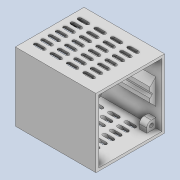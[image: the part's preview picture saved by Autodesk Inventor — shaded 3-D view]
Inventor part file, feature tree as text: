
AUTODESK INVENTOR PART (.ipt)
format: ipt  version: 2021 (Build 250183000, 183)  size: 589,312 bytes
history: native  units: mm
features: extrude x8, sketch x7, projected_geometry x4, plane x3, mirror x2, pattern_linear x1, fillet x1
ambient origin geometry x8: Origin, YZ Plane, XZ Plane, XY Plane, X Axis, Y Axis, Z Axis, Center Point
bodies: Solid1 (feature_tree)
feature tree (26):
  sketch  "Sketch1"  dims[d0=75.0mm d1=75.0mm]
  extrude  "Extrusion1"  Depth=75.0mm
  extrude  "Extrusion2"  TaperAngle=45.0deg  [1 undecoded]
  sketch  "Sketch3"  dims[d2=3.0mm d4=45.0deg]
  plane  "Work Plane1"
  extrude  "Extrusion3"  Depth=60.5mm
  pattern_linear  "Rectangular Pattern1"  Spacing1=85.0mm  [1 undecoded]
  mirror  "Mirror1"
  extrude  "Extrusion4"  Depth=3.0mm TaperAngle=0.0deg
  plane  "Work Plane2"
  sketch  "Sketch7"  dims[d8=56.0mm]
  extrude  "Extrusion5"  Depth=42.5mm
  extrude  "Extrusion6"  [1 undecoded]
  plane  "Work Plane3"
  extrude  "Extrusion8"  Depth=4.0mm
  extrude  "Extrusion9"  Depth=5.0mm
  fillet  "Fillet2"  Radius=33.0mm
  mirror  "Mirror5"
  sketch  "Sketch5"  dims[d5=60.5mm d6=1.8mm]
  sketch  "Sketch6"  dims[d7=1.8mm]
  projected_geometry  "Projected Loop1"
  projected_geometry  "Projected Loop2"
  sketch  "Sketch8"  dims[d9=15.0mm]
  projected_geometry  "Projected Loop3"
  sketch  "Sketch9"  dims[d10=15.0mm d11=85.0mm d12=0.0mm d13=3.0mm d14=0.0mm d16=42.5mm d17=-7.853982mm d19=4.0mm d20=5.0mm d21=33.0mm d22=0.0mm d23=70.0mm d25=8.0mm d26=40.0mm d28=18.0mm d30=33.0mm d31=0.0mm d32=-6.5mm d33=4.3mm d34=5.0mm d35=5.0mm d36=7.2mm d37=8.0mm d38=0.0mm d39=4.0mm d40=0.0mm d41=5.0mm d42=5.0mm d43=7.2mm d44=4.3mm d48=3.0mm d49=3.0mm d50=3.0mm d51=4.0mm d52=0.0mm d54=15.0mm d55=7.5mm d57=4.3mm d58=5.0mm d59=0.0mm d60=5.0mm d61=7.5mm d62=15.0mm d63=4.3mm d64=61.5mm d65=14.0mm]
  projected_geometry  "Projected Loop4"
note: 3 required parameter values undecoded (feature->parameter linkage not recoverable at this tier; creation-order binding heuristic only, values carry confidence <= 0.55)
